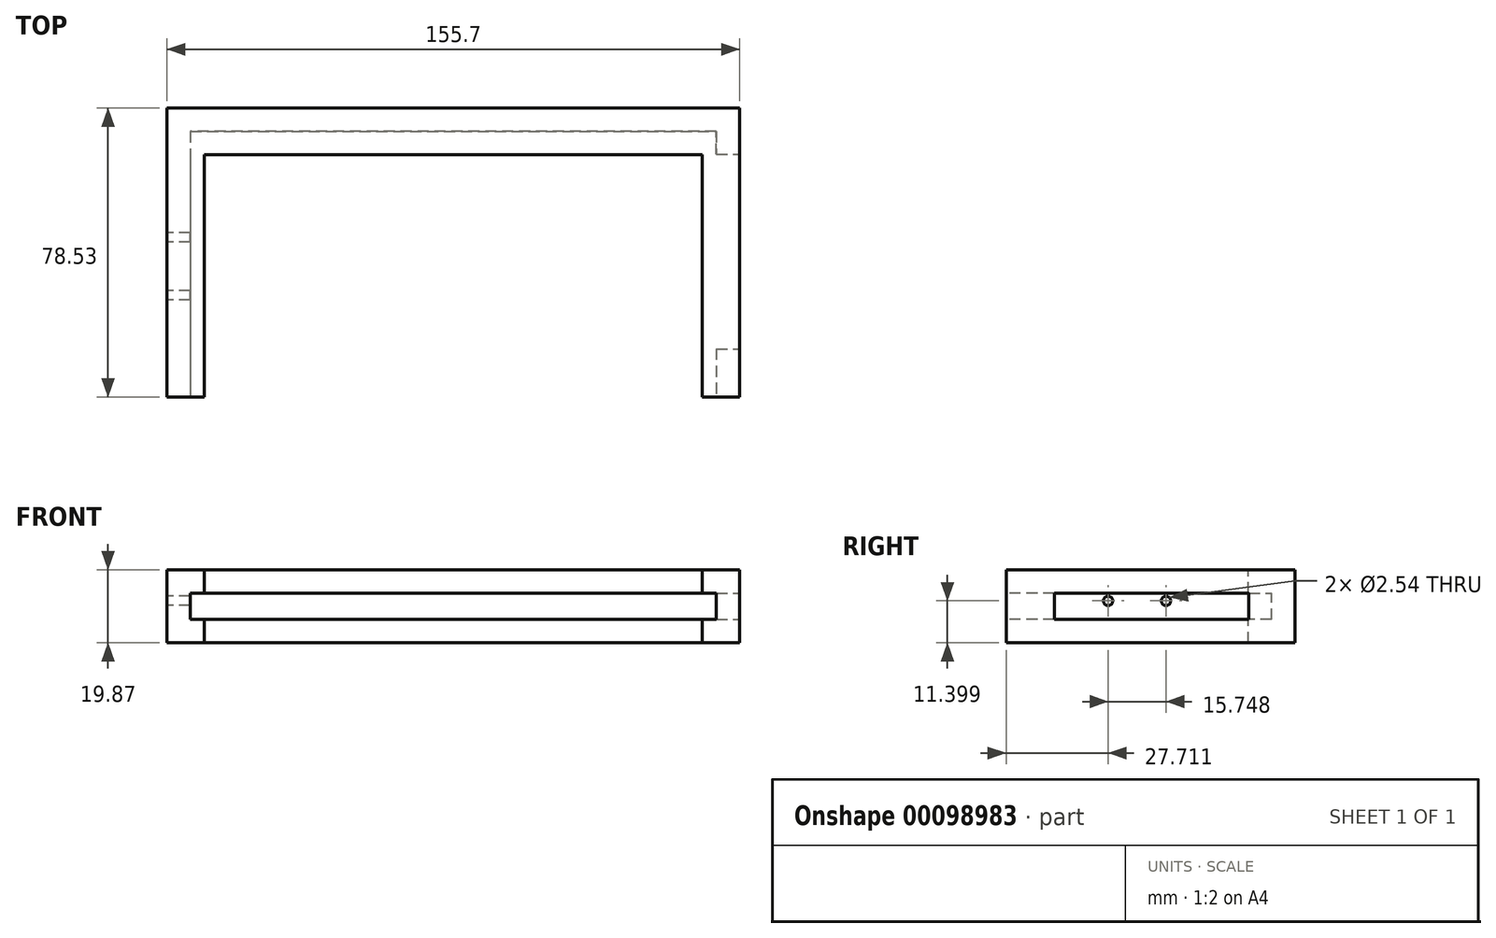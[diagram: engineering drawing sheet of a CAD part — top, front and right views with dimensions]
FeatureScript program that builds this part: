
annotation { "Feature Type Name" : "Feature", "Feature Type Description" : "" }
export const myFeature = defineFeature(function(context is Context, id is Id, definition is map)
    precondition{}
    {
        {
            var Q0;
            Q0=qCreatedBy(makeId("Top.planeOp"),FACE);
            var sketch = newSketch(context, id + "F0", { "sketchPlane" : qUnion([Q0])});
            skLineSegment(sketch, "E0.bottom", {"start": v(71.5, 36.09) * mm, "end": v(-71.5, 36.09) * mm});
            skLineSegment(sketch, "E0.top", {"start": v(71.5, -36.09) * mm, "end": v(-71.5, -36.09) * mm});
            skLineSegment(sketch, "E0.left", {"start": v(71.5, 36.09) * mm, "end": v(71.5, -36.08) * mm});
            skLineSegment(sketch, "E0.right", {"start": v(-71.5, 36.09) * mm, "end": v(-71.5, -36.08) * mm});
            skPoint(sketch, "E0.middle", {"position": v(0, 0) * mm});
            skSolve(sketch);
        }
        {
            var Q0;
            Q0 = qSketchRegion(id + "F0", true);
            extrude(context, id + "F1", {"entities" : qUnion([Q0]), "depth" : 7.17 * mm});
        }
        {
            var Q0;
            Q0=makeQuery(id+"F1.opExtrude","SWEPT_FACE",FACE,{"disambiguationData":[OSD([sQuery(id+"F0.wireOp",EDGE,"E0.right")])]});
            var sketch = newSketch(context, id + "F2", { "sketchPlane" : qUnion([Q0])});
            skLineSegment(sketch, "E1.bottom", {"start": v(-36.09, -6.35) * mm, "end": v(36.08, -6.35) * mm});
            skLineSegment(sketch, "E1.top", {"start": v(-36.09, 13.52) * mm, "end": v(36.08, 13.52) * mm});
            skLineSegment(sketch, "E1.left", {"start": v(-36.09, -6.35) * mm, "end": v(-36.09, 13.52) * mm});
            skLineSegment(sketch, "E1.right", {"start": v(36.08, -6.35) * mm, "end": v(36.08, 13.52) * mm});
            skSolve(sketch);
        }
        {
            var Q0;
            Q0 = qSketchRegion(id + "F2", true);
            extrude(context, id + "F3", {"entities" : qUnion([Q0]), "operationType" : NewBodyOperationType.ADD, "depth" : 6.35 * mm});
        }
        {
            var Q0;
            Q0=makeQuery(id+"F1.opExtrude","SWEPT_FACE",FACE,{"disambiguationData":[OSD([sQuery(id+"F0.wireOp",EDGE,"E0.left")])]});
            var sketch = newSketch(context, id + "F4", { "sketchPlane" : qUnion([Q0])});
            skLineSegment(sketch, "E2.bottom", {"start": v(-36.09, -6.35) * mm, "end": v(36.09, -6.35) * mm});
            skLineSegment(sketch, "E2.top", {"start": v(-36.09, 13.52) * mm, "end": v(36.09, 13.52) * mm});
            skLineSegment(sketch, "E2.left", {"start": v(-36.09, -6.35) * mm, "end": v(-36.09, 13.52) * mm});
            skLineSegment(sketch, "E2.right", {"start": v(36.09, -6.35) * mm, "end": v(36.09, 13.52) * mm});
            skSolve(sketch);
        }
        {
            var Q0;
            Q0 = qSketchRegion(id + "F4", true);
            extrude(context, id + "F5", {"entities" : qUnion([Q0]), "operationType" : NewBodyOperationType.ADD, "depth" : 6.35 * mm});
        }
        {
            var Q0;
            Q0=makeQuery(id+"F1.opExtrude","CAP_FACE",FACE,{"disambiguationData":[OSD([sQuery(id+"F0.wireOp",EDGE,"E0.bottom"),sQuery(id+"F0.wireOp",EDGE,"E0.top"),sQuery(id+"F0.wireOp",EDGE,"E0.left"),sQuery(id+"F0.wireOp",EDGE,"E0.right")])],"isStart":false});
            var sketch = newSketch(context, id + "F6", { "sketchPlane" : qUnion([Q0])});
            skLineSegment(sketch, "E3.bottom", {"start": v(71.5, 36.09) * mm, "end": v(-71.5, 36.09) * mm});
            skLineSegment(sketch, "E3.top", {"start": v(71.5, 29.72) * mm, "end": v(-71.5, 29.72) * mm});
            skLineSegment(sketch, "E3.left", {"start": v(71.5, 36.09) * mm, "end": v(71.5, 29.72) * mm});
            skLineSegment(sketch, "E3.right", {"start": v(-71.5, 36.09) * mm, "end": v(-71.5, 29.72) * mm});
            skSolve(sketch);
        }
        {
            var Q0;
            Q0 = qSketchRegion(id + "F6", true);
            extrude(context, id + "F7", {"entities" : qUnion([Q0]), "operationType" : NewBodyOperationType.ADD, "depth" : 6.35 * mm});
        }
        {
            var Q0;
            Q0=makeQuery(id+"F1.opExtrude","CAP_FACE",FACE,{"disambiguationData":[OSD([sQuery(id+"F0.wireOp",EDGE,"E0.bottom"),sQuery(id+"F0.wireOp",EDGE,"E0.top"),sQuery(id+"F0.wireOp",EDGE,"E0.left"),sQuery(id+"F0.wireOp",EDGE,"E0.right")])],"isStart":true});
            var sketch = newSketch(context, id + "F8", { "sketchPlane" : qUnion([Q0])});
            skLineSegment(sketch, "E4.bottom", {"start": v(-71.5, -36.09) * mm, "end": v(71.5, -36.09) * mm});
            skLineSegment(sketch, "E4.top", {"start": v(-71.5, -29.73) * mm, "end": v(71.5, -29.73) * mm});
            skLineSegment(sketch, "E4.left", {"start": v(-71.5, -36.09) * mm, "end": v(-71.5, -29.73) * mm});
            skLineSegment(sketch, "E4.right", {"start": v(71.5, -36.09) * mm, "end": v(71.5, -29.73) * mm});
            skSolve(sketch);
        }
        {
            var Q0;
            Q0 = qSketchRegion(id + "F8", true);
            extrude(context, id + "F9", {"entities" : qUnion([Q0]), "operationType" : NewBodyOperationType.ADD, "depth" : 6.35 * mm});
        }
        {
            var Q0;
            Q0=makeQuery(id+"F9.boolean.opBoolean","MERGE",FACE,{"derivedFrom":[makeQuery(id+"F7.boolean.opBoolean","MERGE",FACE,{"derivedFrom":[makeQuery(id+"F5.boolean.opBoolean","MERGE",FACE,{"derivedFrom":[makeQuery(id+"F3.boolean.opBoolean","MERGE",FACE,{"derivedFrom":[makeQuery(id+"F1.opExtrude","SWEPT_FACE",FACE,{"disambiguationData":[OSD([sQuery(id+"F0.wireOp",EDGE,"E0.bottom")])]}),makeQuery(id+"F3.opExtrude","SWEPT_FACE",FACE,{"disambiguationData":[OSD([sQuery(id+"F2.wireOp",EDGE,"E1.left")])]})]}),makeQuery(id+"F5.opExtrude","SWEPT_FACE",FACE,{"disambiguationData":[OSD([sQuery(id+"F4.wireOp",EDGE,"E2.right")])]})]}),makeQuery(id+"F7.opExtrude","SWEPT_FACE",FACE,{"disambiguationData":[OSD([sQuery(id+"F6.wireOp",EDGE,"E3.bottom")])]})]}),makeQuery(id+"F9.opExtrude","SWEPT_FACE",FACE,{"disambiguationData":[OSD([sQuery(id+"F8.wireOp",EDGE,"E4.bottom")])]})]});
            var sketch = newSketch(context, id + "F10", { "sketchPlane" : qUnion([Q0])});
            skLineSegment(sketch, "E5.bottom", {"start": v(77.85, 13.52) * mm, "end": v(-77.85, 13.52) * mm});
            skLineSegment(sketch, "E5.top", {"start": v(77.85, -6.35) * mm, "end": v(-77.85, -6.35) * mm});
            skLineSegment(sketch, "E5.left", {"start": v(77.85, 13.52) * mm, "end": v(77.85, -6.35) * mm});
            skLineSegment(sketch, "E5.right", {"start": v(-77.85, 13.52) * mm, "end": v(-77.85, -6.35) * mm});
            skSolve(sketch);
        }
        {
            var Q0;
            Q0 = qSketchRegion(id + "F10", true);
            extrude(context, id + "F11", {"entities" : qUnion([Q0]), "operationType" : NewBodyOperationType.ADD, "depth" : 6.35 * mm});
        }
        {
            var Q0;
            Q0=makeQuery(id+"F5.boolean.opBoolean","MERGE",FACE,{"derivedFrom":[makeQuery(id+"F3.boolean.opBoolean","MERGE",FACE,{"derivedFrom":[makeQuery(id+"F1.opExtrude","SWEPT_FACE",FACE,{"disambiguationData":[OSD([sQuery(id+"F0.wireOp",EDGE,"E0.top")])]}),makeQuery(id+"F3.opExtrude","SWEPT_FACE",FACE,{"disambiguationData":[OSD([sQuery(id+"F2.wireOp",EDGE,"E1.right")])]})]}),makeQuery(id+"F5.opExtrude","SWEPT_FACE",FACE,{"disambiguationData":[OSD([sQuery(id+"F4.wireOp",EDGE,"E2.left")])]})]});
            var sketch = newSketch(context, id + "F12", { "sketchPlane" : qUnion([Q0])});
            skLineSegment(sketch, "E6.bottom", {"start": v(-71.5, 0) * mm, "end": v(71.5, 0) * mm});
            skLineSegment(sketch, "E6.top", {"start": v(-71.5, 7.17) * mm, "end": v(71.5, 7.17) * mm});
            skLineSegment(sketch, "E6.left", {"start": v(-71.5, 0) * mm, "end": v(-71.5, 7.17) * mm});
            skLineSegment(sketch, "E6.right", {"start": v(71.5, 0) * mm, "end": v(71.5, 7.17) * mm});
            skSolve(sketch);
        }
        {
            var Q0;
            Q0 = qSketchRegion(id + "F12", true);
            var Q1;
            Q1=makeQuery(id+"F9.opExtrude","SWEPT_FACE",FACE,{"disambiguationData":[OSD([sQuery(id+"F8.wireOp",EDGE,"E4.top")])]});
            extrude(context, id + "F13", {"entities" : qUnion([Q0]), "operationType" : NewBodyOperationType.REMOVE, "endBound" : BoundingType.UP_TO_SURFACE, "oppositeDirection" : true, "endBoundEntityFace" : qUnion([Q1]), "depth" : 25.4 * mm});
        }
        {
            var Q0;
            {var subQ0=sQuery(id+"F8.wireOp",EDGE,"E4.top");Q0=makeQuery(id+"F13.boolean.opBoolean","MERGE",FACE,{"derivedFrom":[makeQuery(id+"F9.opExtrude","SWEPT_FACE",FACE,{"disambiguationData":[OSD([subQ0])]}),makeQuery(id+"F13.opExtrude","CAP_FACE",FACE,{"disambiguationData":[OSD([subQ0])],"isStart":false})]});}
            var sketch = newSketch(context, id + "F14", { "sketchPlane" : qUnion([Q0])});
            skLineSegment(sketch, "E7.bottom", {"start": v(71.5, 7.17) * mm, "end": v(-71.5, 7.17) * mm});
            skLineSegment(sketch, "E7.top", {"start": v(71.5, 0) * mm, "end": v(-71.5, 0) * mm});
            skLineSegment(sketch, "E7.left", {"start": v(71.5, 7.17) * mm, "end": v(71.5, 0) * mm});
            skLineSegment(sketch, "E7.right", {"start": v(-71.5, 7.17) * mm, "end": v(-71.5, 0) * mm});
            skSolve(sketch);
        }
        {
            var Q0;
            Q0 = qSketchRegion(id + "F14", true);
            extrude(context, id + "F15", {"entities" : qUnion([Q0]), "operationType" : NewBodyOperationType.REMOVE, "oppositeDirection" : true, "depth" : 6.35 * mm});
        }
        {
            var Q0;
            {var subQ8=sQuery(id+"F4.wireOp",EDGE,"E2.bottom");var subQ9=sQuery(id+"F4.wireOp",EDGE,"E2.left");var subQ11=sQuery(id+"F4.wireOp",EDGE,"E2.right");var subQ13=sQuery(id+"F4.wireOp",EDGE,"E2.top");var subQ14=makeQuery(id+"F5.opExtrude","CAP_FACE",FACE,{"disambiguationData":[OSD([subQ8,subQ13,subQ9,subQ11])],"isStart":true});Q0=makeQuery(id+"F15.boolean.opBoolean","MERGE",FACE,{"derivedFrom":[makeQuery(id+"F13.boolean.opBoolean","MERGE",FACE,{"derivedFrom":[makeQuery(id+"F5.boolean.opBoolean","SPLIT",FACE,{"disambiguationData":[TD([makeQuery(id+"F5.opExtrude","SWEPT_FACE",FACE,{"disambiguationData":[OSD([subQ13])]})])],"derivedFrom":subQ14}),makeQuery(id+"F5.boolean.opBoolean","SPLIT",FACE,{"disambiguationData":[TD([makeQuery(id+"F5.opExtrude","SWEPT_FACE",FACE,{"disambiguationData":[OSD([subQ8])]})])],"derivedFrom":subQ14}),makeQuery(id+"F13.opExtrude","SWEPT_FACE",FACE,{"disambiguationData":[OSD([sQuery(id+"F12.wireOp",EDGE,"E6.right")])]})]}),makeQuery(id+"F15.opExtrude","SWEPT_FACE",FACE,{"disambiguationData":[OSD([sQuery(id+"F14.wireOp",EDGE,"E7.left")])]})]});}
            var sketch = newSketch(context, id + "F16", { "sketchPlane" : qUnion([Q0])});
            skLineSegment(sketch, "E8.bottom", {"start": v(-29.73, -6.35) * mm, "end": v(36.08, -6.35) * mm});
            skLineSegment(sketch, "E8.top", {"start": v(-29.73, 0) * mm, "end": v(36.08, 0) * mm});
            skLineSegment(sketch, "E8.left", {"start": v(-29.73, -6.35) * mm, "end": v(-29.73, 0) * mm});
            skLineSegment(sketch, "E8.right", {"start": v(36.09, -6.35) * mm, "end": v(36.09, 0) * mm});
            skSolve(sketch);
        }
        {
            var Q0;
            Q0 = qSketchRegion(id + "F16", true);
            extrude(context, id + "F17", {"entities" : qUnion([Q0]), "operationType" : NewBodyOperationType.ADD, "depth" : 3.8 * mm});
        }
        {
            var Q0;
            {var subQ8=sQuery(id+"F4.wireOp",EDGE,"E2.bottom");var subQ9=sQuery(id+"F4.wireOp",EDGE,"E2.left");var subQ11=sQuery(id+"F4.wireOp",EDGE,"E2.right");var subQ13=sQuery(id+"F4.wireOp",EDGE,"E2.top");var subQ14=makeQuery(id+"F5.opExtrude","CAP_FACE",FACE,{"disambiguationData":[OSD([subQ8,subQ13,subQ9,subQ11])],"isStart":true});Q0=makeQuery(id+"F15.boolean.opBoolean","MERGE",FACE,{"derivedFrom":[makeQuery(id+"F13.boolean.opBoolean","MERGE",FACE,{"derivedFrom":[makeQuery(id+"F5.boolean.opBoolean","SPLIT",FACE,{"disambiguationData":[TD([makeQuery(id+"F5.opExtrude","SWEPT_FACE",FACE,{"disambiguationData":[OSD([subQ13])]})])],"derivedFrom":subQ14}),makeQuery(id+"F5.boolean.opBoolean","SPLIT",FACE,{"disambiguationData":[TD([makeQuery(id+"F5.opExtrude","SWEPT_FACE",FACE,{"disambiguationData":[OSD([subQ8])]})])],"derivedFrom":subQ14}),makeQuery(id+"F13.opExtrude","SWEPT_FACE",FACE,{"disambiguationData":[OSD([sQuery(id+"F12.wireOp",EDGE,"E6.right")])]})]}),makeQuery(id+"F15.opExtrude","SWEPT_FACE",FACE,{"disambiguationData":[OSD([sQuery(id+"F14.wireOp",EDGE,"E7.left")])]})]});}
            var sketch = newSketch(context, id + "F18", { "sketchPlane" : qUnion([Q0])});
            skLineSegment(sketch, "E9.bottom", {"start": v(-29.73, 7.17) * mm, "end": v(36.08, 7.17) * mm});
            skLineSegment(sketch, "E9.top", {"start": v(-29.73, 13.52) * mm, "end": v(36.08, 13.52) * mm});
            skLineSegment(sketch, "E9.left", {"start": v(-29.73, 7.17) * mm, "end": v(-29.73, 13.52) * mm});
            skLineSegment(sketch, "E9.right", {"start": v(36.09, 7.17) * mm, "end": v(36.09, 13.52) * mm});
            skSolve(sketch);
        }
        {
            var Q0;
            Q0 = qSketchRegion(id + "F18", true);
            extrude(context, id + "F19", {"entities" : qUnion([Q0]), "operationType" : NewBodyOperationType.ADD, "depth" : 3.8 * mm});
        }
        {
            var Q0;
            {var subQ2=sQuery(id+"F2.wireOp",EDGE,"E1.bottom");var subQ6=sQuery(id+"F2.wireOp",EDGE,"E1.right");var subQ9=sQuery(id+"F2.wireOp",EDGE,"E1.left");var subQ11=sQuery(id+"F2.wireOp",EDGE,"E1.top");var subQ12=makeQuery(id+"F3.opExtrude","CAP_FACE",FACE,{"disambiguationData":[OSD([subQ2,subQ11,subQ9,subQ6])],"isStart":true});Q0=makeQuery(id+"F15.boolean.opBoolean","MERGE",FACE,{"derivedFrom":[makeQuery(id+"F13.boolean.opBoolean","MERGE",FACE,{"derivedFrom":[makeQuery(id+"F3.boolean.opBoolean","SPLIT",FACE,{"disambiguationData":[TD([makeQuery(id+"F3.opExtrude","SWEPT_FACE",FACE,{"disambiguationData":[OSD([subQ11])]})])],"derivedFrom":subQ12}),makeQuery(id+"F3.boolean.opBoolean","SPLIT",FACE,{"disambiguationData":[TD([makeQuery(id+"F3.opExtrude","SWEPT_FACE",FACE,{"disambiguationData":[OSD([subQ2])]})])],"derivedFrom":subQ12}),makeQuery(id+"F13.opExtrude","SWEPT_FACE",FACE,{"disambiguationData":[OSD([sQuery(id+"F12.wireOp",EDGE,"E6.left")])]})]}),makeQuery(id+"F15.opExtrude","SWEPT_FACE",FACE,{"disambiguationData":[OSD([sQuery(id+"F14.wireOp",EDGE,"E7.right")])]})]});}
            var sketch = newSketch(context, id + "F20", { "sketchPlane" : qUnion([Q0])});
            skLineSegment(sketch, "E10.bottom", {"start": v(29.73, -6.35) * mm, "end": v(-36.08, -6.35) * mm});
            skLineSegment(sketch, "E10.top", {"start": v(29.73, 0) * mm, "end": v(-36.08, 0) * mm});
            skLineSegment(sketch, "E10.left", {"start": v(29.73, -6.35) * mm, "end": v(29.73, 0) * mm});
            skLineSegment(sketch, "E10.right", {"start": v(-36.08, -6.35) * mm, "end": v(-36.08, 0) * mm});
            skSolve(sketch);
        }
        {
            var Q0;
            Q0 = qSketchRegion(id + "F20", true);
            extrude(context, id + "F21", {"entities" : qUnion([Q0]), "operationType" : NewBodyOperationType.ADD, "depth" : 3.8 * mm});
        }
        {
            var Q0;
            {var subQ2=sQuery(id+"F2.wireOp",EDGE,"E1.bottom");var subQ6=sQuery(id+"F2.wireOp",EDGE,"E1.right");var subQ9=sQuery(id+"F2.wireOp",EDGE,"E1.left");var subQ11=sQuery(id+"F2.wireOp",EDGE,"E1.top");var subQ12=makeQuery(id+"F3.opExtrude","CAP_FACE",FACE,{"disambiguationData":[OSD([subQ2,subQ11,subQ9,subQ6])],"isStart":true});Q0=makeQuery(id+"F15.boolean.opBoolean","MERGE",FACE,{"derivedFrom":[makeQuery(id+"F13.boolean.opBoolean","MERGE",FACE,{"derivedFrom":[makeQuery(id+"F3.boolean.opBoolean","SPLIT",FACE,{"disambiguationData":[TD([makeQuery(id+"F3.opExtrude","SWEPT_FACE",FACE,{"disambiguationData":[OSD([subQ11])]})])],"derivedFrom":subQ12}),makeQuery(id+"F3.boolean.opBoolean","SPLIT",FACE,{"disambiguationData":[TD([makeQuery(id+"F3.opExtrude","SWEPT_FACE",FACE,{"disambiguationData":[OSD([subQ2])]})])],"derivedFrom":subQ12}),makeQuery(id+"F13.opExtrude","SWEPT_FACE",FACE,{"disambiguationData":[OSD([sQuery(id+"F12.wireOp",EDGE,"E6.left")])]})]}),makeQuery(id+"F15.opExtrude","SWEPT_FACE",FACE,{"disambiguationData":[OSD([sQuery(id+"F14.wireOp",EDGE,"E7.right")])]})]});}
            var sketch = newSketch(context, id + "F22", { "sketchPlane" : qUnion([Q0])});
            skLineSegment(sketch, "E11.bottom", {"start": v(29.73, 7.17) * mm, "end": v(-36.08, 7.17) * mm});
            skLineSegment(sketch, "E11.top", {"start": v(29.73, 13.52) * mm, "end": v(-36.08, 13.52) * mm});
            skLineSegment(sketch, "E11.left", {"start": v(29.73, 7.17) * mm, "end": v(29.73, 13.52) * mm});
            skLineSegment(sketch, "E11.right", {"start": v(-36.08, 7.17) * mm, "end": v(-36.08, 13.52) * mm});
            skSolve(sketch);
        }
        {
            var Q0;
            Q0 = qSketchRegion(id + "F22", true);
            extrude(context, id + "F23", {"entities" : qUnion([Q0]), "operationType" : NewBodyOperationType.ADD, "depth" : 3.8 * mm});
        }
        {
            var Q0;
            Q0=makeQuery(id+"F11.boolean.opBoolean","MERGE",FACE,{"derivedFrom":[makeQuery(id+"F5.opExtrude","CAP_FACE",FACE,{"disambiguationData":[OSD([sQuery(id+"F4.wireOp",EDGE,"E2.bottom"),sQuery(id+"F4.wireOp",EDGE,"E2.top"),sQuery(id+"F4.wireOp",EDGE,"E2.left"),sQuery(id+"F4.wireOp",EDGE,"E2.right")])],"isStart":false}),makeQuery(id+"F11.opExtrude","SWEPT_FACE",FACE,{"disambiguationData":[OSD([sQuery(id+"F10.wireOp",EDGE,"E5.right")])]})]});
            var sketch = newSketch(context, id + "F24", { "sketchPlane" : qUnion([Q0])});
            skLineSegment(sketch, "E12.bottom", {"start": v(-23, 7.17) * mm, "end": v(29.87, 7.17) * mm});
            skLineSegment(sketch, "E12.top", {"start": v(-23, 0) * mm, "end": v(29.87, 0) * mm});
            skLineSegment(sketch, "E12.left", {"start": v(-23, 7.17) * mm, "end": v(-23, 0) * mm});
            skLineSegment(sketch, "E12.right", {"start": v(29.87, 7.17) * mm, "end": v(29.87, 0) * mm});
            skSolve(sketch);
        }
        {
            var Q0;
            Q0 = qSketchRegion(id + "F24", true);
            extrude(context, id + "F25", {"entities" : qUnion([Q0]), "operationType" : NewBodyOperationType.REMOVE, "oppositeDirection" : true, "depth" : 25.4 * mm});
        }
        {
            var Q0;
            Q0=makeQuery(id+"F11.boolean.opBoolean","MERGE",FACE,{"derivedFrom":[makeQuery(id+"F3.opExtrude","CAP_FACE",FACE,{"disambiguationData":[OSD([sQuery(id+"F2.wireOp",EDGE,"E1.bottom"),sQuery(id+"F2.wireOp",EDGE,"E1.top"),sQuery(id+"F2.wireOp",EDGE,"E1.left"),sQuery(id+"F2.wireOp",EDGE,"E1.right")])],"isStart":false}),makeQuery(id+"F11.opExtrude","SWEPT_FACE",FACE,{"disambiguationData":[OSD([sQuery(id+"F10.wireOp",EDGE,"E5.left")])]})]});
            var sketch = newSketch(context, id + "F26", { "sketchPlane" : qUnion([Q0])});
            skCircle(sketch, "E13", {"center": v(-7.37, 5.05) * mm, "radius": 1.27 * mm});
            skCircle(sketch, "E14", {"center": v(8.38, 5.05) * mm, "radius": 1.27 * mm});
            skSolve(sketch);
        }
        {
            var Q0;
            Q0 = qSketchRegion(id + "F26", true);
            var Q1;
            {var subQ2=sQuery(id+"F2.wireOp",EDGE,"E1.bottom");var subQ6=sQuery(id+"F2.wireOp",EDGE,"E1.right");var subQ9=sQuery(id+"F2.wireOp",EDGE,"E1.left");var subQ11=sQuery(id+"F2.wireOp",EDGE,"E1.top");var subQ12=makeQuery(id+"F3.opExtrude","CAP_FACE",FACE,{"disambiguationData":[OSD([subQ2,subQ11,subQ9,subQ6])],"isStart":true});Q1=makeQuery(id+"F15.boolean.opBoolean","MERGE",FACE,{"derivedFrom":[makeQuery(id+"F13.boolean.opBoolean","MERGE",FACE,{"derivedFrom":[makeQuery(id+"F3.boolean.opBoolean","SPLIT",FACE,{"disambiguationData":[TD([makeQuery(id+"F3.opExtrude","SWEPT_FACE",FACE,{"disambiguationData":[OSD([subQ11])]})])],"derivedFrom":subQ12}),makeQuery(id+"F3.boolean.opBoolean","SPLIT",FACE,{"disambiguationData":[TD([makeQuery(id+"F3.opExtrude","SWEPT_FACE",FACE,{"disambiguationData":[OSD([subQ2])]})])],"derivedFrom":subQ12}),makeQuery(id+"F13.opExtrude","SWEPT_FACE",FACE,{"disambiguationData":[OSD([sQuery(id+"F12.wireOp",EDGE,"E6.left")])]})]}),makeQuery(id+"F15.opExtrude","SWEPT_FACE",FACE,{"disambiguationData":[OSD([sQuery(id+"F14.wireOp",EDGE,"E7.right")])]})]});}
            extrude(context, id + "F27", {"entities" : qUnion([Q0]), "operationType" : NewBodyOperationType.REMOVE, "endBound" : BoundingType.UP_TO_SURFACE, "oppositeDirection" : true, "endBoundEntityFace" : qUnion([Q1]), "depth" : 25.4 * mm});
        }
    });
